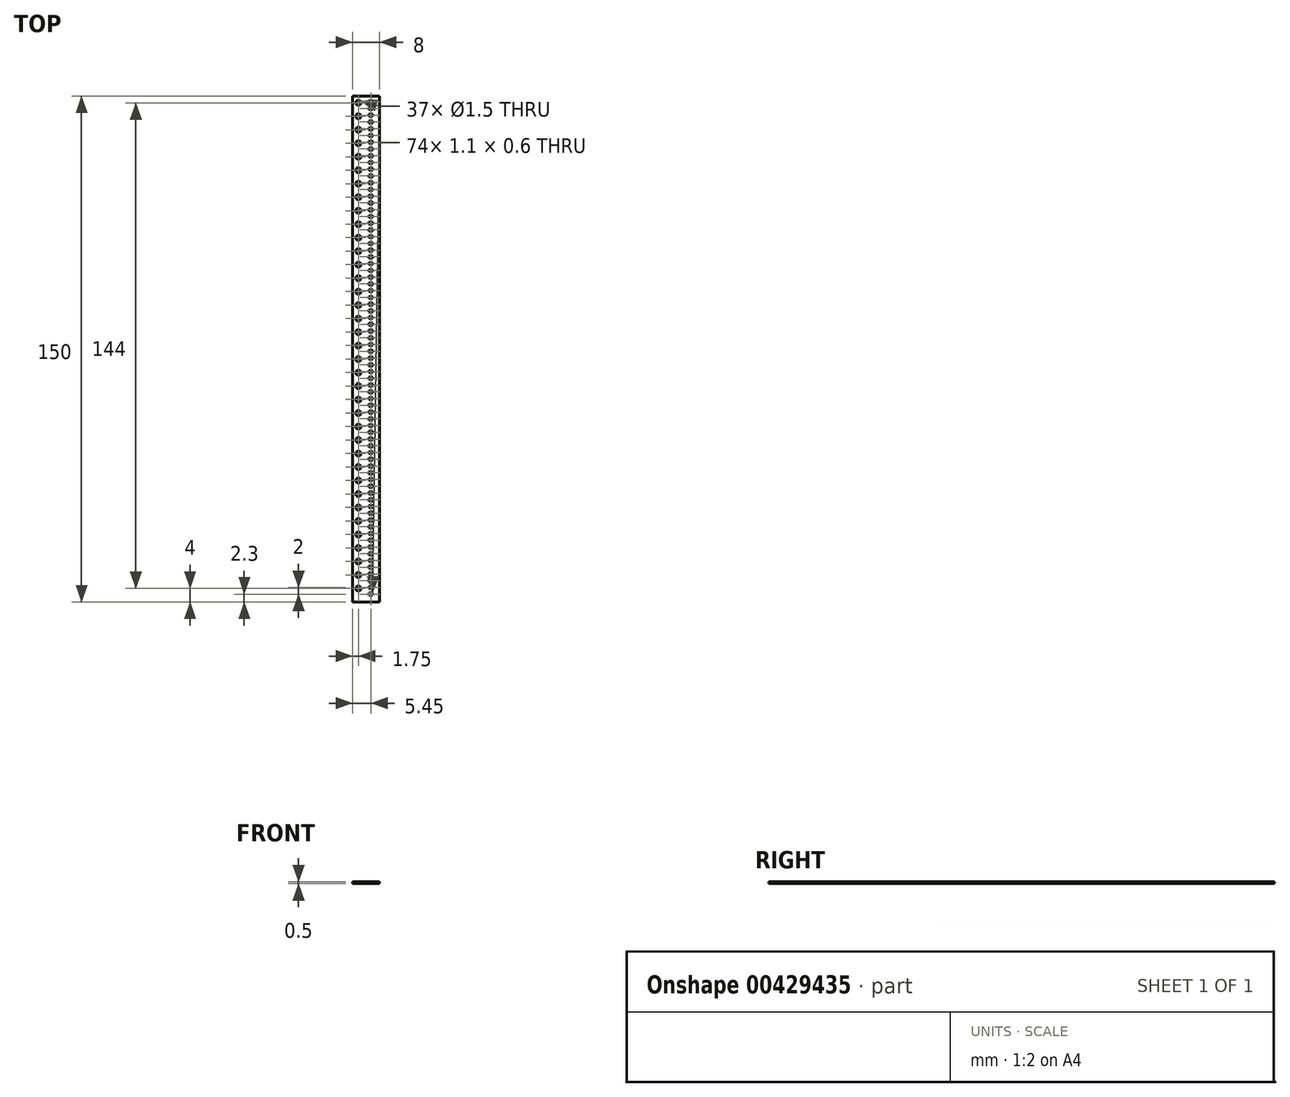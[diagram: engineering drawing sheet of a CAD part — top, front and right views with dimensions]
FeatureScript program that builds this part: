
annotation { "Feature Type Name" : "Feature", "Feature Type Description" : "" }
export const myFeature = defineFeature(function(context is Context, id is Id, definition is map)
    precondition{}
    {
        {
            var Q0;
            Q0=qCreatedBy(makeId("Top.planeOp"),FACE);
            var sketch = newSketch(context, id + "F0", { "sketchPlane" : qUnion([Q0])});
            skLineSegment(sketch, "E0.bottom", {"start": v(0, 150) * mm, "end": v(8, 150) * mm});
            skLineSegment(sketch, "E0.top", {"start": v(0, 0) * mm, "end": v(8, 0) * mm});
            skLineSegment(sketch, "E0.left", {"start": v(0, 150) * mm, "end": v(0, 0) * mm});
            skLineSegment(sketch, "E0.right", {"start": v(8, 150) * mm, "end": v(8, 0) * mm});
            skCircle(sketch, "E1", {"center": v(1.75, 4) * mm, "radius": 0.75 * mm});
            skLineSegment(sketch, "E2.bottom", {"start": v(4.9, 2.6) * mm, "end": v(6, 2.6) * mm});
            skLineSegment(sketch, "E2.top", {"start": v(4.9, 2) * mm, "end": v(6, 2) * mm});
            skLineSegment(sketch, "E2.left", {"start": v(4.9, 2.6) * mm, "end": v(4.9, 2) * mm});
            skLineSegment(sketch, "E2.right", {"start": v(6, 2.6) * mm, "end": v(6, 2) * mm});
            skCircle(sketch, "E3.0.1.0", {"center": v(1.75, 8) * mm, "radius": 0.75 * mm});
            skCircle(sketch, "E3.0.2.0", {"center": v(1.75, 12) * mm, "radius": 0.75 * mm});
            skCircle(sketch, "E3.0.3.0", {"center": v(1.75, 16) * mm, "radius": 0.75 * mm});
            skCircle(sketch, "E3.0.4.0", {"center": v(1.75, 20) * mm, "radius": 0.75 * mm});
            skCircle(sketch, "E3.0.5.0", {"center": v(1.75, 24) * mm, "radius": 0.75 * mm});
            skCircle(sketch, "E3.0.6.0", {"center": v(1.75, 28) * mm, "radius": 0.75 * mm});
            skCircle(sketch, "E3.0.7.0", {"center": v(1.75, 32) * mm, "radius": 0.75 * mm});
            skCircle(sketch, "E3.0.8.0", {"center": v(1.75, 36) * mm, "radius": 0.75 * mm});
            skCircle(sketch, "E3.0.9.0", {"center": v(1.75, 40) * mm, "radius": 0.75 * mm});
            skCircle(sketch, "E3.0.10.0", {"center": v(1.75, 44) * mm, "radius": 0.75 * mm});
            skCircle(sketch, "E3.0.11.0", {"center": v(1.75, 48) * mm, "radius": 0.75 * mm});
            skCircle(sketch, "E3.0.12.0", {"center": v(1.75, 52) * mm, "radius": 0.75 * mm});
            skCircle(sketch, "E3.0.13.0", {"center": v(1.75, 56) * mm, "radius": 0.75 * mm});
            skCircle(sketch, "E3.0.14.0", {"center": v(1.75, 60) * mm, "radius": 0.75 * mm});
            skCircle(sketch, "E3.0.15.0", {"center": v(1.75, 64) * mm, "radius": 0.75 * mm});
            skCircle(sketch, "E3.0.16.0", {"center": v(1.75, 68) * mm, "radius": 0.75 * mm});
            skCircle(sketch, "E3.0.17.0", {"center": v(1.75, 72) * mm, "radius": 0.75 * mm});
            skCircle(sketch, "E3.0.18.0", {"center": v(1.75, 76) * mm, "radius": 0.75 * mm});
            skCircle(sketch, "E3.0.19.0", {"center": v(1.75, 80) * mm, "radius": 0.75 * mm});
            skCircle(sketch, "E3.0.20.0", {"center": v(1.75, 84) * mm, "radius": 0.75 * mm});
            skCircle(sketch, "E3.0.21.0", {"center": v(1.75, 88) * mm, "radius": 0.75 * mm});
            skCircle(sketch, "E3.0.22.0", {"center": v(1.75, 92) * mm, "radius": 0.75 * mm});
            skCircle(sketch, "E3.0.23.0", {"center": v(1.75, 96) * mm, "radius": 0.75 * mm});
            skCircle(sketch, "E3.0.24.0", {"center": v(1.75, 100) * mm, "radius": 0.75 * mm});
            skCircle(sketch, "E3.0.25.0", {"center": v(1.75, 104) * mm, "radius": 0.75 * mm});
            skCircle(sketch, "E3.0.26.0", {"center": v(1.75, 108) * mm, "radius": 0.75 * mm});
            skCircle(sketch, "E3.0.27.0", {"center": v(1.75, 112) * mm, "radius": 0.75 * mm});
            skCircle(sketch, "E3.0.28.0", {"center": v(1.75, 116) * mm, "radius": 0.75 * mm});
            skCircle(sketch, "E3.0.29.0", {"center": v(1.75, 120) * mm, "radius": 0.75 * mm});
            skCircle(sketch, "E3.0.30.0", {"center": v(1.75, 124) * mm, "radius": 0.75 * mm});
            skCircle(sketch, "E3.0.31.0", {"center": v(1.75, 128) * mm, "radius": 0.75 * mm});
            skCircle(sketch, "E3.0.32.0", {"center": v(1.75, 132) * mm, "radius": 0.75 * mm});
            skCircle(sketch, "E3.0.33.0", {"center": v(1.75, 136) * mm, "radius": 0.75 * mm});
            skCircle(sketch, "E3.0.34.0", {"center": v(1.75, 140) * mm, "radius": 0.75 * mm});
            skLineSegment(sketch, "E3.direction1", {"start": v(1.75, 4) * mm, "end": v(26.75, 4) * mm, "construction": true});
            skLineSegment(sketch, "E3.direction2", {"start": v(1.75, 4) * mm, "end": v(1.75, 8) * mm, "construction": true});
            skLineSegment(sketch, "E4.0.1.0", {"start": v(4.9, 4.6) * mm, "end": v(6, 4.6) * mm});
            skLineSegment(sketch, "E4.0.1.1", {"start": v(4.9, 4) * mm, "end": v(6, 4) * mm});
            skLineSegment(sketch, "E4.0.1.2", {"start": v(4.9, 4.6) * mm, "end": v(4.9, 4) * mm});
            skLineSegment(sketch, "E4.0.1.3", {"start": v(6, 4.6) * mm, "end": v(6, 4) * mm});
            skLineSegment(sketch, "E4.0.2.0", {"start": v(4.9, 6.6) * mm, "end": v(6, 6.6) * mm});
            skLineSegment(sketch, "E4.0.2.1", {"start": v(4.9, 6) * mm, "end": v(6, 6) * mm});
            skLineSegment(sketch, "E4.0.2.2", {"start": v(4.9, 6.6) * mm, "end": v(4.9, 6) * mm});
            skLineSegment(sketch, "E4.0.2.3", {"start": v(6, 6.6) * mm, "end": v(6, 6) * mm});
            skLineSegment(sketch, "E4.0.3.0", {"start": v(4.9, 8.6) * mm, "end": v(6, 8.6) * mm});
            skLineSegment(sketch, "E4.0.3.1", {"start": v(4.9, 8) * mm, "end": v(6, 8) * mm});
            skLineSegment(sketch, "E4.0.3.2", {"start": v(4.9, 8.6) * mm, "end": v(4.9, 8) * mm});
            skLineSegment(sketch, "E4.0.3.3", {"start": v(6, 8.6) * mm, "end": v(6, 8) * mm});
            skLineSegment(sketch, "E4.0.4.0", {"start": v(4.9, 10.6) * mm, "end": v(6, 10.6) * mm});
            skLineSegment(sketch, "E4.0.4.1", {"start": v(4.9, 10) * mm, "end": v(6, 10) * mm});
            skLineSegment(sketch, "E4.0.4.2", {"start": v(4.9, 10.6) * mm, "end": v(4.9, 10) * mm});
            skLineSegment(sketch, "E4.0.4.3", {"start": v(6, 10.6) * mm, "end": v(6, 10) * mm});
            skLineSegment(sketch, "E4.0.5.0", {"start": v(4.9, 12.6) * mm, "end": v(6, 12.6) * mm});
            skLineSegment(sketch, "E4.0.5.1", {"start": v(4.9, 12) * mm, "end": v(6, 12) * mm});
            skLineSegment(sketch, "E4.0.5.2", {"start": v(4.9, 12.6) * mm, "end": v(4.9, 12) * mm});
            skLineSegment(sketch, "E4.0.5.3", {"start": v(6, 12.6) * mm, "end": v(6, 12) * mm});
            skLineSegment(sketch, "E4.0.6.0", {"start": v(4.9, 14.6) * mm, "end": v(6, 14.6) * mm});
            skLineSegment(sketch, "E4.0.6.1", {"start": v(4.9, 14) * mm, "end": v(6, 14) * mm});
            skLineSegment(sketch, "E4.0.6.2", {"start": v(4.9, 14.6) * mm, "end": v(4.9, 14) * mm});
            skLineSegment(sketch, "E4.0.6.3", {"start": v(6, 14.6) * mm, "end": v(6, 14) * mm});
            skLineSegment(sketch, "E4.0.7.0", {"start": v(4.9, 16.6) * mm, "end": v(6, 16.6) * mm});
            skLineSegment(sketch, "E4.0.7.1", {"start": v(4.9, 16) * mm, "end": v(6, 16) * mm});
            skLineSegment(sketch, "E4.0.7.2", {"start": v(4.9, 16.6) * mm, "end": v(4.9, 16) * mm});
            skLineSegment(sketch, "E4.0.7.3", {"start": v(6, 16.6) * mm, "end": v(6, 16) * mm});
            skLineSegment(sketch, "E4.0.8.0", {"start": v(4.9, 18.6) * mm, "end": v(6, 18.6) * mm});
            skLineSegment(sketch, "E4.0.8.1", {"start": v(4.9, 18) * mm, "end": v(6, 18) * mm});
            skLineSegment(sketch, "E4.0.8.2", {"start": v(4.9, 18.6) * mm, "end": v(4.9, 18) * mm});
            skLineSegment(sketch, "E4.0.8.3", {"start": v(6, 18.6) * mm, "end": v(6, 18) * mm});
            skLineSegment(sketch, "E4.0.9.0", {"start": v(4.9, 20.6) * mm, "end": v(6, 20.6) * mm});
            skLineSegment(sketch, "E4.0.9.1", {"start": v(4.9, 20) * mm, "end": v(6, 20) * mm});
            skLineSegment(sketch, "E4.0.9.2", {"start": v(4.9, 20.6) * mm, "end": v(4.9, 20) * mm});
            skLineSegment(sketch, "E4.0.9.3", {"start": v(6, 20.6) * mm, "end": v(6, 20) * mm});
            skLineSegment(sketch, "E4.0.10.0", {"start": v(4.9, 22.6) * mm, "end": v(6, 22.6) * mm});
            skLineSegment(sketch, "E4.0.10.1", {"start": v(4.9, 22) * mm, "end": v(6, 22) * mm});
            skLineSegment(sketch, "E4.0.10.2", {"start": v(4.9, 22.6) * mm, "end": v(4.9, 22) * mm});
            skLineSegment(sketch, "E4.0.10.3", {"start": v(6, 22.6) * mm, "end": v(6, 22) * mm});
            skLineSegment(sketch, "E4.0.11.0", {"start": v(4.9, 24.6) * mm, "end": v(6, 24.6) * mm});
            skLineSegment(sketch, "E4.0.11.1", {"start": v(4.9, 24) * mm, "end": v(6, 24) * mm});
            skLineSegment(sketch, "E4.0.11.2", {"start": v(4.9, 24.6) * mm, "end": v(4.9, 24) * mm});
            skLineSegment(sketch, "E4.0.11.3", {"start": v(6, 24.6) * mm, "end": v(6, 24) * mm});
            skLineSegment(sketch, "E4.0.12.0", {"start": v(4.9, 26.6) * mm, "end": v(6, 26.6) * mm});
            skLineSegment(sketch, "E4.0.12.1", {"start": v(4.9, 26) * mm, "end": v(6, 26) * mm});
            skLineSegment(sketch, "E4.0.12.2", {"start": v(4.9, 26.6) * mm, "end": v(4.9, 26) * mm});
            skLineSegment(sketch, "E4.0.12.3", {"start": v(6, 26.6) * mm, "end": v(6, 26) * mm});
            skLineSegment(sketch, "E4.0.13.0", {"start": v(4.9, 28.6) * mm, "end": v(6, 28.6) * mm});
            skLineSegment(sketch, "E4.0.13.1", {"start": v(4.9, 28) * mm, "end": v(6, 28) * mm});
            skLineSegment(sketch, "E4.0.13.2", {"start": v(4.9, 28.6) * mm, "end": v(4.9, 28) * mm});
            skLineSegment(sketch, "E4.0.13.3", {"start": v(6, 28.6) * mm, "end": v(6, 28) * mm});
            skLineSegment(sketch, "E4.0.14.0", {"start": v(4.9, 30.6) * mm, "end": v(6, 30.6) * mm});
            skLineSegment(sketch, "E4.0.14.1", {"start": v(4.9, 30) * mm, "end": v(6, 30) * mm});
            skLineSegment(sketch, "E4.0.14.2", {"start": v(4.9, 30.6) * mm, "end": v(4.9, 30) * mm});
            skLineSegment(sketch, "E4.0.14.3", {"start": v(6, 30.6) * mm, "end": v(6, 30) * mm});
            skLineSegment(sketch, "E4.0.15.0", {"start": v(4.9, 32.6) * mm, "end": v(6, 32.6) * mm});
            skLineSegment(sketch, "E4.0.15.1", {"start": v(4.9, 32) * mm, "end": v(6, 32) * mm});
            skLineSegment(sketch, "E4.0.15.2", {"start": v(4.9, 32.6) * mm, "end": v(4.9, 32) * mm});
            skLineSegment(sketch, "E4.0.15.3", {"start": v(6, 32.6) * mm, "end": v(6, 32) * mm});
            skLineSegment(sketch, "E4.0.16.0", {"start": v(4.9, 34.6) * mm, "end": v(6, 34.6) * mm});
            skLineSegment(sketch, "E4.0.16.1", {"start": v(4.9, 34) * mm, "end": v(6, 34) * mm});
            skLineSegment(sketch, "E4.0.16.2", {"start": v(4.9, 34.6) * mm, "end": v(4.9, 34) * mm});
            skLineSegment(sketch, "E4.0.16.3", {"start": v(6, 34.6) * mm, "end": v(6, 34) * mm});
            skLineSegment(sketch, "E4.0.17.0", {"start": v(4.9, 36.6) * mm, "end": v(6, 36.6) * mm});
            skLineSegment(sketch, "E4.0.17.1", {"start": v(4.9, 36) * mm, "end": v(6, 36) * mm});
            skLineSegment(sketch, "E4.0.17.2", {"start": v(4.9, 36.6) * mm, "end": v(4.9, 36) * mm});
            skLineSegment(sketch, "E4.0.17.3", {"start": v(6, 36.6) * mm, "end": v(6, 36) * mm});
            skLineSegment(sketch, "E4.0.18.0", {"start": v(4.9, 38.6) * mm, "end": v(6, 38.6) * mm});
            skLineSegment(sketch, "E4.0.18.1", {"start": v(4.9, 38) * mm, "end": v(6, 38) * mm});
            skLineSegment(sketch, "E4.0.18.2", {"start": v(4.9, 38.6) * mm, "end": v(4.9, 38) * mm});
            skLineSegment(sketch, "E4.0.18.3", {"start": v(6, 38.6) * mm, "end": v(6, 38) * mm});
            skLineSegment(sketch, "E4.0.19.0", {"start": v(4.9, 40.6) * mm, "end": v(6, 40.6) * mm});
            skLineSegment(sketch, "E4.0.19.1", {"start": v(4.9, 40) * mm, "end": v(6, 40) * mm});
            skLineSegment(sketch, "E4.0.19.2", {"start": v(4.9, 40.6) * mm, "end": v(4.9, 40) * mm});
            skLineSegment(sketch, "E4.0.19.3", {"start": v(6, 40.6) * mm, "end": v(6, 40) * mm});
            skLineSegment(sketch, "E4.0.20.0", {"start": v(4.9, 42.6) * mm, "end": v(6, 42.6) * mm});
            skLineSegment(sketch, "E4.0.20.1", {"start": v(4.9, 42) * mm, "end": v(6, 42) * mm});
            skLineSegment(sketch, "E4.0.20.2", {"start": v(4.9, 42.6) * mm, "end": v(4.9, 42) * mm});
            skLineSegment(sketch, "E4.0.20.3", {"start": v(6, 42.6) * mm, "end": v(6, 42) * mm});
            skLineSegment(sketch, "E4.0.21.0", {"start": v(4.9, 44.6) * mm, "end": v(6, 44.6) * mm});
            skLineSegment(sketch, "E4.0.21.1", {"start": v(4.9, 44) * mm, "end": v(6, 44) * mm});
            skLineSegment(sketch, "E4.0.21.2", {"start": v(4.9, 44.6) * mm, "end": v(4.9, 44) * mm});
            skLineSegment(sketch, "E4.0.21.3", {"start": v(6, 44.6) * mm, "end": v(6, 44) * mm});
            skLineSegment(sketch, "E4.0.22.0", {"start": v(4.9, 46.6) * mm, "end": v(6, 46.6) * mm});
            skLineSegment(sketch, "E4.0.22.1", {"start": v(4.9, 46) * mm, "end": v(6, 46) * mm});
            skLineSegment(sketch, "E4.0.22.2", {"start": v(4.9, 46.6) * mm, "end": v(4.9, 46) * mm});
            skLineSegment(sketch, "E4.0.22.3", {"start": v(6, 46.6) * mm, "end": v(6, 46) * mm});
            skLineSegment(sketch, "E4.0.23.0", {"start": v(4.9, 48.6) * mm, "end": v(6, 48.6) * mm});
            skLineSegment(sketch, "E4.0.23.1", {"start": v(4.9, 48) * mm, "end": v(6, 48) * mm});
            skLineSegment(sketch, "E4.0.23.2", {"start": v(4.9, 48.6) * mm, "end": v(4.9, 48) * mm});
            skLineSegment(sketch, "E4.0.23.3", {"start": v(6, 48.6) * mm, "end": v(6, 48) * mm});
            skLineSegment(sketch, "E4.0.24.0", {"start": v(4.9, 50.6) * mm, "end": v(6, 50.6) * mm});
            skLineSegment(sketch, "E4.0.24.1", {"start": v(4.9, 50) * mm, "end": v(6, 50) * mm});
            skLineSegment(sketch, "E4.0.24.2", {"start": v(4.9, 50.6) * mm, "end": v(4.9, 50) * mm});
            skLineSegment(sketch, "E4.0.24.3", {"start": v(6, 50.6) * mm, "end": v(6, 50) * mm});
            skLineSegment(sketch, "E4.0.25.0", {"start": v(4.9, 52.6) * mm, "end": v(6, 52.6) * mm});
            skLineSegment(sketch, "E4.0.25.1", {"start": v(4.9, 52) * mm, "end": v(6, 52) * mm});
            skLineSegment(sketch, "E4.0.25.2", {"start": v(4.9, 52.6) * mm, "end": v(4.9, 52) * mm});
            skLineSegment(sketch, "E4.0.25.3", {"start": v(6, 52.6) * mm, "end": v(6, 52) * mm});
            skLineSegment(sketch, "E4.0.26.0", {"start": v(4.9, 54.6) * mm, "end": v(6, 54.6) * mm});
            skLineSegment(sketch, "E4.0.26.1", {"start": v(4.9, 54) * mm, "end": v(6, 54) * mm});
            skLineSegment(sketch, "E4.0.26.2", {"start": v(4.9, 54.6) * mm, "end": v(4.9, 54) * mm});
            skLineSegment(sketch, "E4.0.26.3", {"start": v(6, 54.6) * mm, "end": v(6, 54) * mm});
            skLineSegment(sketch, "E4.0.27.0", {"start": v(4.9, 56.6) * mm, "end": v(6, 56.6) * mm});
            skLineSegment(sketch, "E4.0.27.1", {"start": v(4.9, 56) * mm, "end": v(6, 56) * mm});
            skLineSegment(sketch, "E4.0.27.2", {"start": v(4.9, 56.6) * mm, "end": v(4.9, 56) * mm});
            skLineSegment(sketch, "E4.0.27.3", {"start": v(6, 56.6) * mm, "end": v(6, 56) * mm});
            skLineSegment(sketch, "E4.0.28.0", {"start": v(4.9, 58.6) * mm, "end": v(6, 58.6) * mm});
            skLineSegment(sketch, "E4.0.28.1", {"start": v(4.9, 58) * mm, "end": v(6, 58) * mm});
            skLineSegment(sketch, "E4.0.28.2", {"start": v(4.9, 58.6) * mm, "end": v(4.9, 58) * mm});
            skLineSegment(sketch, "E4.0.28.3", {"start": v(6, 58.6) * mm, "end": v(6, 58) * mm});
            skLineSegment(sketch, "E4.0.29.0", {"start": v(4.9, 60.6) * mm, "end": v(6, 60.6) * mm});
            skLineSegment(sketch, "E4.0.29.1", {"start": v(4.9, 60) * mm, "end": v(6, 60) * mm});
            skLineSegment(sketch, "E4.0.29.2", {"start": v(4.9, 60.6) * mm, "end": v(4.9, 60) * mm});
            skLineSegment(sketch, "E4.0.29.3", {"start": v(6, 60.6) * mm, "end": v(6, 60) * mm});
            skLineSegment(sketch, "E4.0.30.0", {"start": v(4.9, 62.6) * mm, "end": v(6, 62.6) * mm});
            skLineSegment(sketch, "E4.0.30.1", {"start": v(4.9, 62) * mm, "end": v(6, 62) * mm});
            skLineSegment(sketch, "E4.0.30.2", {"start": v(4.9, 62.6) * mm, "end": v(4.9, 62) * mm});
            skLineSegment(sketch, "E4.0.30.3", {"start": v(6, 62.6) * mm, "end": v(6, 62) * mm});
            skLineSegment(sketch, "E4.0.31.0", {"start": v(4.9, 64.6) * mm, "end": v(6, 64.6) * mm});
            skLineSegment(sketch, "E4.0.31.1", {"start": v(4.9, 64) * mm, "end": v(6, 64) * mm});
            skLineSegment(sketch, "E4.0.31.2", {"start": v(4.9, 64.6) * mm, "end": v(4.9, 64) * mm});
            skLineSegment(sketch, "E4.0.31.3", {"start": v(6, 64.6) * mm, "end": v(6, 64) * mm});
            skLineSegment(sketch, "E4.0.32.0", {"start": v(4.9, 66.6) * mm, "end": v(6, 66.6) * mm});
            skLineSegment(sketch, "E4.0.32.1", {"start": v(4.9, 66) * mm, "end": v(6, 66) * mm});
            skLineSegment(sketch, "E4.0.32.2", {"start": v(4.9, 66.6) * mm, "end": v(4.9, 66) * mm});
            skLineSegment(sketch, "E4.0.32.3", {"start": v(6, 66.6) * mm, "end": v(6, 66) * mm});
            skLineSegment(sketch, "E4.0.33.0", {"start": v(4.9, 68.6) * mm, "end": v(6, 68.6) * mm});
            skLineSegment(sketch, "E4.0.33.1", {"start": v(4.9, 68) * mm, "end": v(6, 68) * mm});
            skLineSegment(sketch, "E4.0.33.2", {"start": v(4.9, 68.6) * mm, "end": v(4.9, 68) * mm});
            skLineSegment(sketch, "E4.0.33.3", {"start": v(6, 68.6) * mm, "end": v(6, 68) * mm});
            skLineSegment(sketch, "E4.0.34.0", {"start": v(4.9, 70.6) * mm, "end": v(6, 70.6) * mm});
            skLineSegment(sketch, "E4.0.34.1", {"start": v(4.9, 70) * mm, "end": v(6, 70) * mm});
            skLineSegment(sketch, "E4.0.34.2", {"start": v(4.9, 70.6) * mm, "end": v(4.9, 70) * mm});
            skLineSegment(sketch, "E4.0.34.3", {"start": v(6, 70.6) * mm, "end": v(6, 70) * mm});
            skLineSegment(sketch, "E4.0.35.0", {"start": v(4.9, 72.6) * mm, "end": v(6, 72.6) * mm});
            skLineSegment(sketch, "E4.0.35.1", {"start": v(4.9, 72) * mm, "end": v(6, 72) * mm});
            skLineSegment(sketch, "E4.0.35.2", {"start": v(4.9, 72.6) * mm, "end": v(4.9, 72) * mm});
            skLineSegment(sketch, "E4.0.35.3", {"start": v(6, 72.6) * mm, "end": v(6, 72) * mm});
            skLineSegment(sketch, "E4.0.36.0", {"start": v(4.9, 74.6) * mm, "end": v(6, 74.6) * mm});
            skLineSegment(sketch, "E4.0.36.1", {"start": v(4.9, 74) * mm, "end": v(6, 74) * mm});
            skLineSegment(sketch, "E4.0.36.2", {"start": v(4.9, 74.6) * mm, "end": v(4.9, 74) * mm});
            skLineSegment(sketch, "E4.0.36.3", {"start": v(6, 74.6) * mm, "end": v(6, 74) * mm});
            skLineSegment(sketch, "E4.0.37.0", {"start": v(4.9, 76.6) * mm, "end": v(6, 76.6) * mm});
            skLineSegment(sketch, "E4.0.37.1", {"start": v(4.9, 76) * mm, "end": v(6, 76) * mm});
            skLineSegment(sketch, "E4.0.37.2", {"start": v(4.9, 76.6) * mm, "end": v(4.9, 76) * mm});
            skLineSegment(sketch, "E4.0.37.3", {"start": v(6, 76.6) * mm, "end": v(6, 76) * mm});
            skLineSegment(sketch, "E4.0.38.0", {"start": v(4.9, 78.6) * mm, "end": v(6, 78.6) * mm});
            skLineSegment(sketch, "E4.0.38.1", {"start": v(4.9, 78) * mm, "end": v(6, 78) * mm});
            skLineSegment(sketch, "E4.0.38.2", {"start": v(4.9, 78.6) * mm, "end": v(4.9, 78) * mm});
            skLineSegment(sketch, "E4.0.38.3", {"start": v(6, 78.6) * mm, "end": v(6, 78) * mm});
            skLineSegment(sketch, "E4.0.39.0", {"start": v(4.9, 80.6) * mm, "end": v(6, 80.6) * mm});
            skLineSegment(sketch, "E4.0.39.1", {"start": v(4.9, 80) * mm, "end": v(6, 80) * mm});
            skLineSegment(sketch, "E4.0.39.2", {"start": v(4.9, 80.6) * mm, "end": v(4.9, 80) * mm});
            skLineSegment(sketch, "E4.0.39.3", {"start": v(6, 80.6) * mm, "end": v(6, 80) * mm});
            skLineSegment(sketch, "E4.0.40.0", {"start": v(4.9, 82.6) * mm, "end": v(6, 82.6) * mm});
            skLineSegment(sketch, "E4.0.40.1", {"start": v(4.9, 82) * mm, "end": v(6, 82) * mm});
            skLineSegment(sketch, "E4.0.40.2", {"start": v(4.9, 82.6) * mm, "end": v(4.9, 82) * mm});
            skLineSegment(sketch, "E4.0.40.3", {"start": v(6, 82.6) * mm, "end": v(6, 82) * mm});
            skLineSegment(sketch, "E4.0.41.0", {"start": v(4.9, 84.6) * mm, "end": v(6, 84.6) * mm});
            skLineSegment(sketch, "E4.0.41.1", {"start": v(4.9, 84) * mm, "end": v(6, 84) * mm});
            skLineSegment(sketch, "E4.0.41.2", {"start": v(4.9, 84.6) * mm, "end": v(4.9, 84) * mm});
            skLineSegment(sketch, "E4.0.41.3", {"start": v(6, 84.6) * mm, "end": v(6, 84) * mm});
            skLineSegment(sketch, "E4.0.42.0", {"start": v(4.9, 86.6) * mm, "end": v(6, 86.6) * mm});
            skLineSegment(sketch, "E4.0.42.1", {"start": v(4.9, 86) * mm, "end": v(6, 86) * mm});
            skLineSegment(sketch, "E4.0.42.2", {"start": v(4.9, 86.6) * mm, "end": v(4.9, 86) * mm});
            skLineSegment(sketch, "E4.0.42.3", {"start": v(6, 86.6) * mm, "end": v(6, 86) * mm});
            skLineSegment(sketch, "E4.0.43.0", {"start": v(4.9, 88.6) * mm, "end": v(6, 88.6) * mm});
            skLineSegment(sketch, "E4.0.43.1", {"start": v(4.9, 88) * mm, "end": v(6, 88) * mm});
            skLineSegment(sketch, "E4.0.43.2", {"start": v(4.9, 88.6) * mm, "end": v(4.9, 88) * mm});
            skLineSegment(sketch, "E4.0.43.3", {"start": v(6, 88.6) * mm, "end": v(6, 88) * mm});
            skLineSegment(sketch, "E4.0.44.0", {"start": v(4.9, 90.6) * mm, "end": v(6, 90.6) * mm});
            skLineSegment(sketch, "E4.0.44.1", {"start": v(4.9, 90) * mm, "end": v(6, 90) * mm});
            skLineSegment(sketch, "E4.0.44.2", {"start": v(4.9, 90.6) * mm, "end": v(4.9, 90) * mm});
            skLineSegment(sketch, "E4.0.44.3", {"start": v(6, 90.6) * mm, "end": v(6, 90) * mm});
            skLineSegment(sketch, "E4.0.45.0", {"start": v(4.9, 92.6) * mm, "end": v(6, 92.6) * mm});
            skLineSegment(sketch, "E4.0.45.1", {"start": v(4.9, 92) * mm, "end": v(6, 92) * mm});
            skLineSegment(sketch, "E4.0.45.2", {"start": v(4.9, 92.6) * mm, "end": v(4.9, 92) * mm});
            skLineSegment(sketch, "E4.0.45.3", {"start": v(6, 92.6) * mm, "end": v(6, 92) * mm});
            skLineSegment(sketch, "E4.0.46.0", {"start": v(4.9, 94.6) * mm, "end": v(6, 94.6) * mm});
            skLineSegment(sketch, "E4.0.46.1", {"start": v(4.9, 94) * mm, "end": v(6, 94) * mm});
            skLineSegment(sketch, "E4.0.46.2", {"start": v(4.9, 94.6) * mm, "end": v(4.9, 94) * mm});
            skLineSegment(sketch, "E4.0.46.3", {"start": v(6, 94.6) * mm, "end": v(6, 94) * mm});
            skLineSegment(sketch, "E4.0.47.0", {"start": v(4.9, 96.6) * mm, "end": v(6, 96.6) * mm});
            skLineSegment(sketch, "E4.0.47.1", {"start": v(4.9, 96) * mm, "end": v(6, 96) * mm});
            skLineSegment(sketch, "E4.0.47.2", {"start": v(4.9, 96.6) * mm, "end": v(4.9, 96) * mm});
            skLineSegment(sketch, "E4.0.47.3", {"start": v(6, 96.6) * mm, "end": v(6, 96) * mm});
            skLineSegment(sketch, "E4.0.48.0", {"start": v(4.9, 98.6) * mm, "end": v(6, 98.6) * mm});
            skLineSegment(sketch, "E4.0.48.1", {"start": v(4.9, 98) * mm, "end": v(6, 98) * mm});
            skLineSegment(sketch, "E4.0.48.2", {"start": v(4.9, 98.6) * mm, "end": v(4.9, 98) * mm});
            skLineSegment(sketch, "E4.0.48.3", {"start": v(6, 98.6) * mm, "end": v(6, 98) * mm});
            skLineSegment(sketch, "E4.0.49.0", {"start": v(4.9, 100.6) * mm, "end": v(6, 100.6) * mm});
            skLineSegment(sketch, "E4.0.49.1", {"start": v(4.9, 100) * mm, "end": v(6, 100) * mm});
            skLineSegment(sketch, "E4.0.49.2", {"start": v(4.9, 100.6) * mm, "end": v(4.9, 100) * mm});
            skLineSegment(sketch, "E4.0.49.3", {"start": v(6, 100.6) * mm, "end": v(6, 100) * mm});
            skLineSegment(sketch, "E4.direction1", {"start": v(4.9, 2) * mm, "end": v(29.9, 2) * mm, "construction": true});
            skLineSegment(sketch, "E4.direction2", {"start": v(4.9, 2) * mm, "end": v(4.9, 4) * mm, "construction": true});
            skCircle(sketch, "E5.0.0.35", {"center": v(1.75, 144) * mm, "radius": 0.75 * mm});
            skCircle(sketch, "E5.0.0.36", {"center": v(1.75, 148) * mm, "radius": 0.75 * mm});
            skLineSegment(sketch, "E6.0.0.50", {"start": v(4.9, 102.6) * mm, "end": v(6, 102.6) * mm});
            skLineSegment(sketch, "E6.3.0.50", {"start": v(4.9, 102) * mm, "end": v(6, 102) * mm});
            skLineSegment(sketch, "E6.6.0.50", {"start": v(4.9, 102.6) * mm, "end": v(4.9, 102) * mm});
            skLineSegment(sketch, "E6.9.0.50", {"start": v(6, 102.6) * mm, "end": v(6, 102) * mm});
            skLineSegment(sketch, "E6.0.0.51", {"start": v(4.9, 104.6) * mm, "end": v(6, 104.6) * mm});
            skLineSegment(sketch, "E6.3.0.51", {"start": v(4.9, 104) * mm, "end": v(6, 104) * mm});
            skLineSegment(sketch, "E6.6.0.51", {"start": v(4.9, 104.6) * mm, "end": v(4.9, 104) * mm});
            skLineSegment(sketch, "E6.9.0.51", {"start": v(6, 104.6) * mm, "end": v(6, 104) * mm});
            skLineSegment(sketch, "E6.0.0.52", {"start": v(4.9, 106.6) * mm, "end": v(6, 106.6) * mm});
            skLineSegment(sketch, "E6.3.0.52", {"start": v(4.9, 106) * mm, "end": v(6, 106) * mm});
            skLineSegment(sketch, "E6.6.0.52", {"start": v(4.9, 106.6) * mm, "end": v(4.9, 106) * mm});
            skLineSegment(sketch, "E6.9.0.52", {"start": v(6, 106.6) * mm, "end": v(6, 106) * mm});
            skLineSegment(sketch, "E6.0.0.53", {"start": v(4.9, 108.6) * mm, "end": v(6, 108.6) * mm});
            skLineSegment(sketch, "E6.3.0.53", {"start": v(4.9, 108) * mm, "end": v(6, 108) * mm});
            skLineSegment(sketch, "E6.6.0.53", {"start": v(4.9, 108.6) * mm, "end": v(4.9, 108) * mm});
            skLineSegment(sketch, "E6.9.0.53", {"start": v(6, 108.6) * mm, "end": v(6, 108) * mm});
            skLineSegment(sketch, "E6.0.0.54", {"start": v(4.9, 110.6) * mm, "end": v(6, 110.6) * mm});
            skLineSegment(sketch, "E6.3.0.54", {"start": v(4.9, 110) * mm, "end": v(6, 110) * mm});
            skLineSegment(sketch, "E6.6.0.54", {"start": v(4.9, 110.6) * mm, "end": v(4.9, 110) * mm});
            skLineSegment(sketch, "E6.9.0.54", {"start": v(6, 110.6) * mm, "end": v(6, 110) * mm});
            skLineSegment(sketch, "E6.0.0.55", {"start": v(4.9, 112.6) * mm, "end": v(6, 112.6) * mm});
            skLineSegment(sketch, "E6.3.0.55", {"start": v(4.9, 112) * mm, "end": v(6, 112) * mm});
            skLineSegment(sketch, "E6.6.0.55", {"start": v(4.9, 112.6) * mm, "end": v(4.9, 112) * mm});
            skLineSegment(sketch, "E6.9.0.55", {"start": v(6, 112.6) * mm, "end": v(6, 112) * mm});
            skLineSegment(sketch, "E6.0.0.56", {"start": v(4.9, 114.6) * mm, "end": v(6, 114.6) * mm});
            skLineSegment(sketch, "E6.3.0.56", {"start": v(4.9, 114) * mm, "end": v(6, 114) * mm});
            skLineSegment(sketch, "E6.6.0.56", {"start": v(4.9, 114.6) * mm, "end": v(4.9, 114) * mm});
            skLineSegment(sketch, "E6.9.0.56", {"start": v(6, 114.6) * mm, "end": v(6, 114) * mm});
            skLineSegment(sketch, "E6.0.0.57", {"start": v(4.9, 116.6) * mm, "end": v(6, 116.6) * mm});
            skLineSegment(sketch, "E6.3.0.57", {"start": v(4.9, 116) * mm, "end": v(6, 116) * mm});
            skLineSegment(sketch, "E6.6.0.57", {"start": v(4.9, 116.6) * mm, "end": v(4.9, 116) * mm});
            skLineSegment(sketch, "E6.9.0.57", {"start": v(6, 116.6) * mm, "end": v(6, 116) * mm});
            skLineSegment(sketch, "E6.0.0.58", {"start": v(4.9, 118.6) * mm, "end": v(6, 118.6) * mm});
            skLineSegment(sketch, "E6.3.0.58", {"start": v(4.9, 118) * mm, "end": v(6, 118) * mm});
            skLineSegment(sketch, "E6.6.0.58", {"start": v(4.9, 118.6) * mm, "end": v(4.9, 118) * mm});
            skLineSegment(sketch, "E6.9.0.58", {"start": v(6, 118.6) * mm, "end": v(6, 118) * mm});
            skLineSegment(sketch, "E6.0.0.59", {"start": v(4.9, 120.6) * mm, "end": v(6, 120.6) * mm});
            skLineSegment(sketch, "E6.3.0.59", {"start": v(4.9, 120) * mm, "end": v(6, 120) * mm});
            skLineSegment(sketch, "E6.6.0.59", {"start": v(4.9, 120.6) * mm, "end": v(4.9, 120) * mm});
            skLineSegment(sketch, "E6.9.0.59", {"start": v(6, 120.6) * mm, "end": v(6, 120) * mm});
            skLineSegment(sketch, "E6.0.0.60", {"start": v(4.9, 122.6) * mm, "end": v(6, 122.6) * mm});
            skLineSegment(sketch, "E6.3.0.60", {"start": v(4.9, 122) * mm, "end": v(6, 122) * mm});
            skLineSegment(sketch, "E6.6.0.60", {"start": v(4.9, 122.6) * mm, "end": v(4.9, 122) * mm});
            skLineSegment(sketch, "E6.9.0.60", {"start": v(6, 122.6) * mm, "end": v(6, 122) * mm});
            skLineSegment(sketch, "E6.0.0.61", {"start": v(4.9, 124.6) * mm, "end": v(6, 124.6) * mm});
            skLineSegment(sketch, "E6.3.0.61", {"start": v(4.9, 124) * mm, "end": v(6, 124) * mm});
            skLineSegment(sketch, "E6.6.0.61", {"start": v(4.9, 124.6) * mm, "end": v(4.9, 124) * mm});
            skLineSegment(sketch, "E6.9.0.61", {"start": v(6, 124.6) * mm, "end": v(6, 124) * mm});
            skLineSegment(sketch, "E6.0.0.62", {"start": v(4.9, 126.6) * mm, "end": v(6, 126.6) * mm});
            skLineSegment(sketch, "E6.3.0.62", {"start": v(4.9, 126) * mm, "end": v(6, 126) * mm});
            skLineSegment(sketch, "E6.6.0.62", {"start": v(4.9, 126.6) * mm, "end": v(4.9, 126) * mm});
            skLineSegment(sketch, "E6.9.0.62", {"start": v(6, 126.6) * mm, "end": v(6, 126) * mm});
            skLineSegment(sketch, "E6.0.0.63", {"start": v(4.9, 128.6) * mm, "end": v(6, 128.6) * mm});
            skLineSegment(sketch, "E6.3.0.63", {"start": v(4.9, 128) * mm, "end": v(6, 128) * mm});
            skLineSegment(sketch, "E6.6.0.63", {"start": v(4.9, 128.6) * mm, "end": v(4.9, 128) * mm});
            skLineSegment(sketch, "E6.9.0.63", {"start": v(6, 128.6) * mm, "end": v(6, 128) * mm});
            skLineSegment(sketch, "E6.0.0.64", {"start": v(4.9, 130.6) * mm, "end": v(6, 130.6) * mm});
            skLineSegment(sketch, "E6.3.0.64", {"start": v(4.9, 130) * mm, "end": v(6, 130) * mm});
            skLineSegment(sketch, "E6.6.0.64", {"start": v(4.9, 130.6) * mm, "end": v(4.9, 130) * mm});
            skLineSegment(sketch, "E6.9.0.64", {"start": v(6, 130.6) * mm, "end": v(6, 130) * mm});
            skLineSegment(sketch, "E6.0.0.65", {"start": v(4.9, 132.6) * mm, "end": v(6, 132.6) * mm});
            skLineSegment(sketch, "E6.3.0.65", {"start": v(4.9, 132) * mm, "end": v(6, 132) * mm});
            skLineSegment(sketch, "E6.6.0.65", {"start": v(4.9, 132.6) * mm, "end": v(4.9, 132) * mm});
            skLineSegment(sketch, "E6.9.0.65", {"start": v(6, 132.6) * mm, "end": v(6, 132) * mm});
            skLineSegment(sketch, "E6.0.0.66", {"start": v(4.9, 134.6) * mm, "end": v(6, 134.6) * mm});
            skLineSegment(sketch, "E6.3.0.66", {"start": v(4.9, 134) * mm, "end": v(6, 134) * mm});
            skLineSegment(sketch, "E6.6.0.66", {"start": v(4.9, 134.6) * mm, "end": v(4.9, 134) * mm});
            skLineSegment(sketch, "E6.9.0.66", {"start": v(6, 134.6) * mm, "end": v(6, 134) * mm});
            skLineSegment(sketch, "E6.0.0.67", {"start": v(4.9, 136.6) * mm, "end": v(6, 136.6) * mm});
            skLineSegment(sketch, "E6.3.0.67", {"start": v(4.9, 136) * mm, "end": v(6, 136) * mm});
            skLineSegment(sketch, "E6.6.0.67", {"start": v(4.9, 136.6) * mm, "end": v(4.9, 136) * mm});
            skLineSegment(sketch, "E6.9.0.67", {"start": v(6, 136.6) * mm, "end": v(6, 136) * mm});
            skLineSegment(sketch, "E6.0.0.68", {"start": v(4.9, 138.6) * mm, "end": v(6, 138.6) * mm});
            skLineSegment(sketch, "E6.3.0.68", {"start": v(4.9, 138) * mm, "end": v(6, 138) * mm});
            skLineSegment(sketch, "E6.6.0.68", {"start": v(4.9, 138.6) * mm, "end": v(4.9, 138) * mm});
            skLineSegment(sketch, "E6.9.0.68", {"start": v(6, 138.6) * mm, "end": v(6, 138) * mm});
            skLineSegment(sketch, "E6.0.0.69", {"start": v(4.9, 140.6) * mm, "end": v(6, 140.6) * mm});
            skLineSegment(sketch, "E6.3.0.69", {"start": v(4.9, 140) * mm, "end": v(6, 140) * mm});
            skLineSegment(sketch, "E6.6.0.69", {"start": v(4.9, 140.6) * mm, "end": v(4.9, 140) * mm});
            skLineSegment(sketch, "E6.9.0.69", {"start": v(6, 140.6) * mm, "end": v(6, 140) * mm});
            skLineSegment(sketch, "E6.0.0.70", {"start": v(4.9, 142.6) * mm, "end": v(6, 142.6) * mm});
            skLineSegment(sketch, "E6.3.0.70", {"start": v(4.9, 142) * mm, "end": v(6, 142) * mm});
            skLineSegment(sketch, "E6.6.0.70", {"start": v(4.9, 142.6) * mm, "end": v(4.9, 142) * mm});
            skLineSegment(sketch, "E6.9.0.70", {"start": v(6, 142.6) * mm, "end": v(6, 142) * mm});
            skLineSegment(sketch, "E6.0.0.71", {"start": v(4.9, 144.6) * mm, "end": v(6, 144.6) * mm});
            skLineSegment(sketch, "E6.3.0.71", {"start": v(4.9, 144) * mm, "end": v(6, 144) * mm});
            skLineSegment(sketch, "E6.6.0.71", {"start": v(4.9, 144.6) * mm, "end": v(4.9, 144) * mm});
            skLineSegment(sketch, "E6.9.0.71", {"start": v(6, 144.6) * mm, "end": v(6, 144) * mm});
            skLineSegment(sketch, "E7.0.0.72", {"start": v(4.9, 146.6) * mm, "end": v(6, 146.6) * mm});
            skLineSegment(sketch, "E7.3.0.72", {"start": v(4.9, 146) * mm, "end": v(6, 146) * mm});
            skLineSegment(sketch, "E7.6.0.72", {"start": v(4.9, 146.6) * mm, "end": v(4.9, 146) * mm});
            skLineSegment(sketch, "E7.9.0.72", {"start": v(6, 146.6) * mm, "end": v(6, 146) * mm});
            skLineSegment(sketch, "E7.0.0.73", {"start": v(4.9, 148.6) * mm, "end": v(6, 148.6) * mm});
            skLineSegment(sketch, "E7.3.0.73", {"start": v(4.9, 148) * mm, "end": v(6, 148) * mm});
            skLineSegment(sketch, "E7.6.0.73", {"start": v(4.9, 148.6) * mm, "end": v(4.9, 148) * mm});
            skLineSegment(sketch, "E7.9.0.73", {"start": v(6, 148.6) * mm, "end": v(6, 148) * mm});
            skSolve(sketch);
        }
        {
            var Q0;
            Q0=makeQuery(id+"F0.imprint","IMPRINT",FACE,{"disambiguationData":[TD([[makeQuery(id+"F0.imprint","IMPRINT",EDGE,{"derivedFrom":sQuery(id+"F0.wireOp",EDGE,"E0.bottom")}),-1.0]])]});
            extrude(context, id + "F1", {"entities" : qUnion([Q0]), "depth" : 0.5 * mm});
        }
    });
